# Revit family: QF_ELECTROLUXPROFESSIONAL_1LSPHR_TD6-45SLD_S
name_source: partatom
category: Attrezzature speciali
units: mm (PartAtom-declared; Revit-internal decimal feet)

## family parameters
Basato su piano di lavoro = No
Condiviso = No
Punto di calcolo locali = No
Quota connettore circolare = Usa diametro
Sempre verticale = Sì
Taglio con vuoti quando caricato = No
Tipo di parte = Normale

## types (3) — shared parameters
ALL_MODEL_IMAGE = <Nessuno>
Cold Water Size = 0 mm
Compressed Air Pressure = 0.0 Pa
Compressed Air Size = 0 mm
Compressed Air Volume = 0.0 L/s
Condensate Return Size = 25 mm
Cycle = 50 Hz
Descrizione = TUMBLE DRYER DRUM VOLUME 900L CAPACITY 45KG/100LB SLIDING DOOR
Direct Waste Size = 0 mm
Gas Size = 0 mm
Hot Water Size = 0 mm
Phase = 3
Produttore = Electrolux Professional
Steam Supply Maximum Pressure = 1000.0 Pa
Steam Supply Minimum Pressure = 100.0 Pa
Steam Supply Size = 25 mm
URL = https://www.electroluxprofessional.com
Volts = 380 V
Watts = 3 W
zero-valued in all types: Gas KW, Prospetto di default, Steam Pounds per Hour

## per-type parameters (varying)
| type | Depth Actual | Height Actual | Item Number | Length Actual | Weight in Pounds |
| 1L0HDK | 1300 mm  [stored 4.26509 ft] | 2465 mm  [stored 8.08727 ft] | 9875030029 | 1314 mm  [stored 4.31102 ft] | 494 |
| 1L82BD | 1305 mm  [stored 4.2815 ft] | 2550 mm  [stored 8.36614 ft] | 9875030016 | 1320 mm  [stored 4.33071 ft] | 546 |
| 1L99A4 | 1305 mm  [stored 4.2815 ft] | 2550 mm  [stored 8.36614 ft] | 9875030036 | 1320 mm  [stored 4.33071 ft] | 546 |

note: [stored X ft] marks values corroborated as IEEE doubles in the binary element streams (Revit-internal decimal feet)

## geometry (parser evidence)
native form markers: Blend x2, Sweep x2
no freeform markers — native parametric forms only
